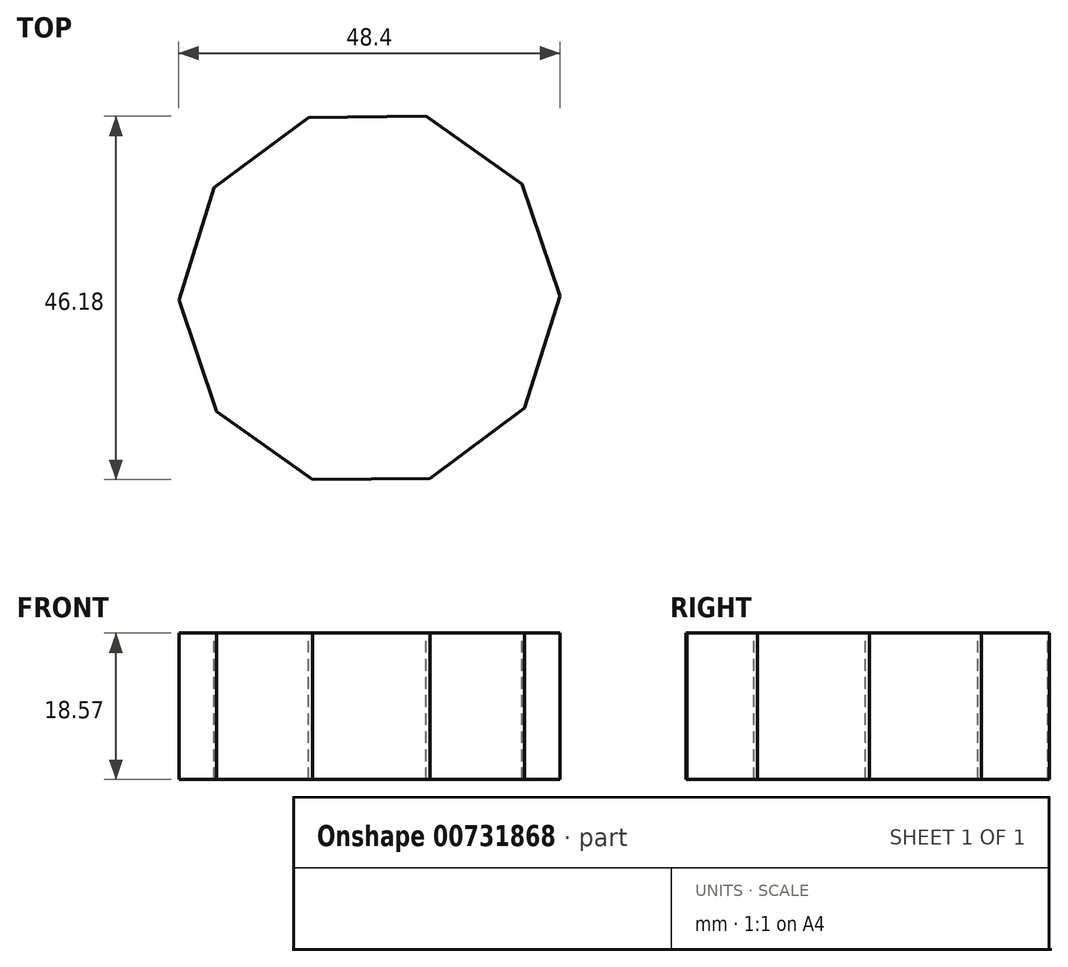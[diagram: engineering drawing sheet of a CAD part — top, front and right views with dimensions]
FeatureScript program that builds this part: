
annotation { "Feature Type Name" : "Feature", "Feature Type Description" : "" }
export const myFeature = defineFeature(function(context is Context, id is Id, definition is map)
    precondition{}
    {
        {
            var Q0;
            Q0=qCreatedBy(makeId("Top.planeOp"),FACE);
            var sketch = newSketch(context, id + "F0", { "sketchPlane" : qUnion([Q0])});
            skCircle(sketch, "E0.cCircle", {"center": v(0, 0) * mm, "radius": 23.01 * mm, "construction": true});
            skLineSegment(sketch, "E0.0", {"start": v(19.73, -14) * mm, "end": v(7.73, -22.93) * mm});
            skLineSegment(sketch, "E0.1", {"start": v(7.73, -22.93) * mm, "end": v(-7.23, -23.1) * mm});
            skLineSegment(sketch, "E0.2", {"start": v(-7.23, -23.1) * mm, "end": v(-19.42, -14.44) * mm});
            skLineSegment(sketch, "E0.3", {"start": v(-19.42, -14.44) * mm, "end": v(-24.2, -0.26) * mm});
            skLineSegment(sketch, "E0.4", {"start": v(-24.2, -0.26) * mm, "end": v(-19.73, 14) * mm});
            skLineSegment(sketch, "E0.5", {"start": v(-19.73, 14) * mm, "end": v(-7.73, 22.93) * mm});
            skLineSegment(sketch, "E0.6", {"start": v(-7.73, 22.93) * mm, "end": v(7.23, 23.1) * mm});
            skLineSegment(sketch, "E0.7", {"start": v(7.23, 23.1) * mm, "end": v(19.42, 14.44) * mm});
            skLineSegment(sketch, "E0.8", {"start": v(19.42, 14.44) * mm, "end": v(24.2, 0.26) * mm});
            skLineSegment(sketch, "E0.9", {"start": v(24.2, 0.26) * mm, "end": v(19.73, -14) * mm});
            skPoint(sketch, "E0.0.midPoint", {"position": v(13.73, -18.47) * mm});
            skSolve(sketch);
        }
        {
            var Q0;
            Q0 = qSketchRegion(id + "F0", true);
            extrude(context, id + "F1", {"entities" : qUnion([Q0]), "oppositeDirection" : true, "depth" : 18.57 * mm, "offsetDistance" : 25.4 * mm});
        }
    });
